# Revit family: Deca_Acabamento para Registro de Gaveta Prata_4900.C.50.PQ
name_source: partatom
category: Plumbing Fixtures
revit_build: Autodesk Revit Architecture 2012 (Build: 20120126_0600(x64)
units: mm (PartAtom-declared; Revit-internal decimal feet)

## types (3) — shared parameters
Acabamento = Deca CR10 Cromado Metal
Aprovado por = Contino/quattroD
Assembly Code = D2020
Atendimento ao Cliente = 0800-0117073
Consumo = Varia com a pressão
Criado por = Contino/quattroD
Código = 4900.C50.PQ
Description = Acabamento para registro
Flow Pressure = 0.00 psi
Linha = Prata
Louça/Metais = Metal
Manufacturer = Deca
Material = Deca_Latão Cromado e Plástico de Engenharia
Model = 4900.C50.PQ
Norma = ABNT NBR 10283: 2003
Peso Liquido (Kg) = 0.2
Pressão = 2 A 40 mca
Produto = Acabamento para registro de gaveta Prata
Segmento = Competitivo
URL = www.deca.com.br/produtos
Variações de COR = Cromado 1/2, 3/4 e 1 (4900.C50.PQ)
zero-valued in all types: CWFU, Default Elevation

## per-type parameters (varying)
| type | Base de Registro de Gaveta_Family | Diâmetro Ponto de Agua | Raio Ponto de Agua |
| 4900.C50.PQ_Cromado CR10_1/2" | Deca_Acabamento para Registro de Gaveta Prata_4900.C50.PQ : 4509.102 - DN 15 (1/2") | 15 mm  [stored 0.0492126 ft] | 8 mm  [stored 0.0262467 ft] |
| 4900.C50.PQ_Cromado CR10_3/4" | Deca_Acabamento para Registro de Gaveta Prata_4900.C50.PQ : 4509.202 - DN 20 (3/4") | 20 mm  [stored 0.0656168 ft] | 10 mm  [stored 0.0328084 ft] |
| 4900.C50.PQ_Cromado CR10_1" | Deca_Acabamento para Registro de Gaveta Prata_4900.C50.PQ : 4509.302 - DN 25 (1") | 25 mm  [stored 0.082021 ft] | 13 mm |

note: [stored X ft] marks values corroborated as IEEE doubles in the binary element streams (Revit-internal decimal feet)

## geometry (parser evidence)
native form markers: Blend x6, Sweep x5
no freeform markers — native parametric forms only
